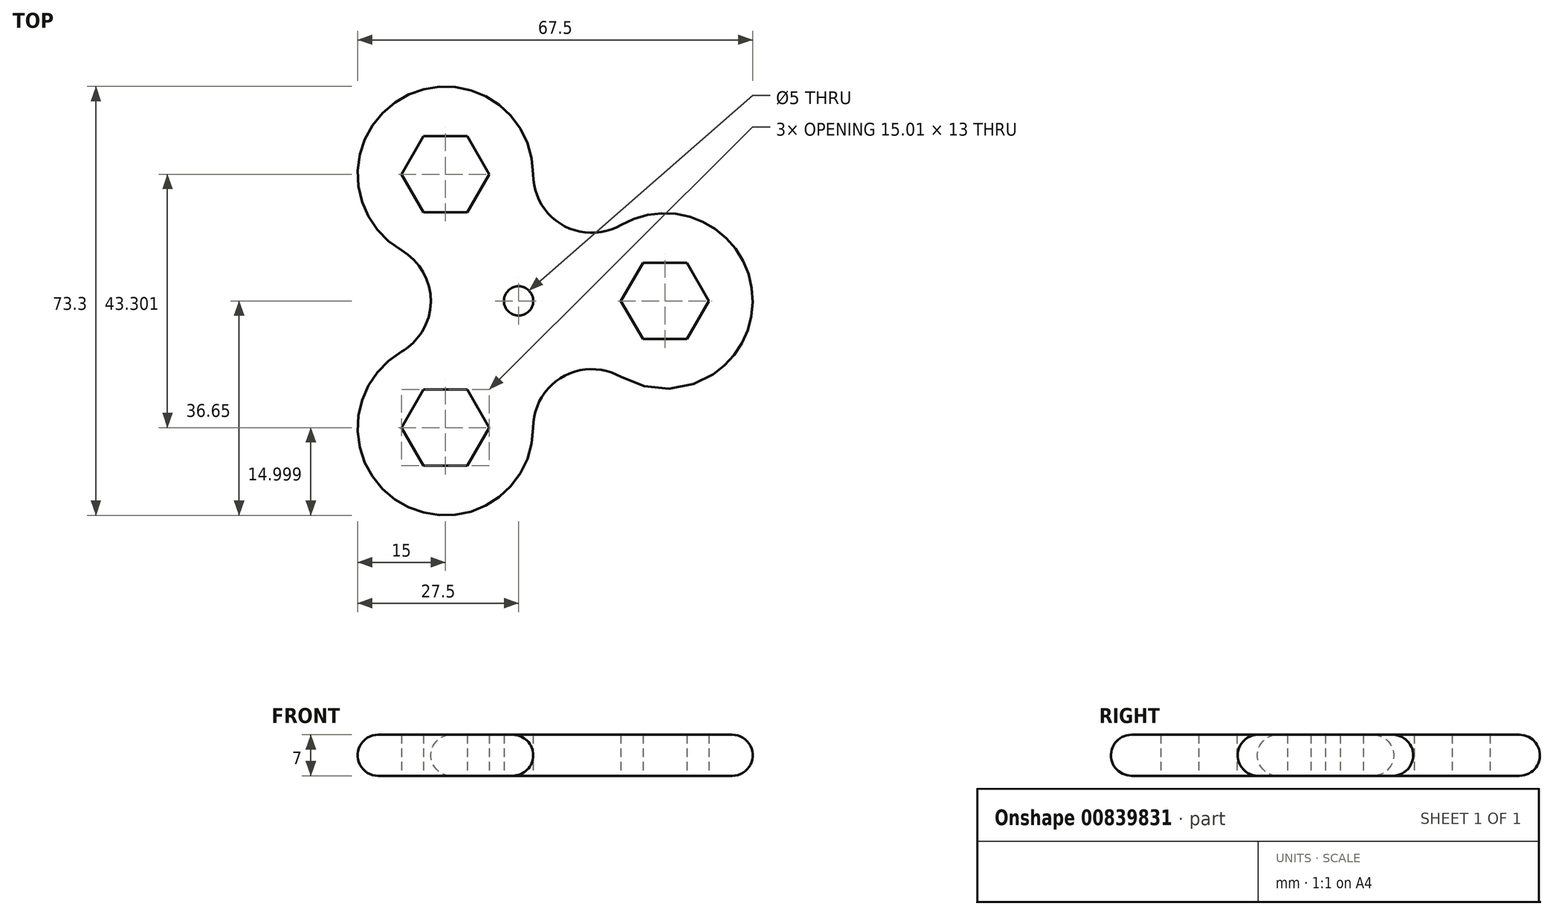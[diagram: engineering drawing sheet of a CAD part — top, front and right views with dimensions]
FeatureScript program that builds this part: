
annotation { "Feature Type Name" : "Feature", "Feature Type Description" : "" }
export const myFeature = defineFeature(function(context is Context, id is Id, definition is map)
    precondition{}
    {
        {
            var Q0;
            Q0=qCreatedBy(makeId("Top.planeOp"),FACE);
            var sketch = newSketch(context, id + "F0", { "sketchPlane" : qUnion([Q0])});
            skLineSegment(sketch, "E0", {"start": v(0, 0) * mm, "end": v(25, 0) * mm, "construction": true});
            skArc(sketch, "E1", {"start": v(17.5, -13) * mm, "mid": v(40, 0) * mm, "end": v(17.5, 13) * mm});
            skArc(sketch, "E2.1.1", {"start": v(2.5, 21.65) * mm, "mid": v(-20, 34.64) * mm, "end": v(-20, 8.66) * mm});
            skLineSegment(sketch, "E2.1.2", {"start": v(0, 0) * mm, "end": v(-12.5, 21.65) * mm, "construction": true});
            skArc(sketch, "E2.2.1", {"start": v(-20, -8.66) * mm, "mid": v(-20, -34.64) * mm, "end": v(2.5, -21.65) * mm});
            skLineSegment(sketch, "E2.2.2", {"start": v(0, 0) * mm, "end": v(-12.5, -21.65) * mm, "construction": true});
            skPoint(sketch, "E2.center", {"position": v(0, 0) * mm});
            skArc(sketch, "E3", {"start": v(2.5, 21.65) * mm, "mid": v(7.5, 13) * mm, "end": v(17.5, 13) * mm});
            skArc(sketch, "E4.1.0", {"start": v(-20, -8.66) * mm, "mid": v(-15, 0) * mm, "end": v(-20, 8.66) * mm});
            skArc(sketch, "E4.2.0", {"start": v(17.5, -13) * mm, "mid": v(7.5, -13) * mm, "end": v(2.5, -21.65) * mm});
            skCircle(sketch, "E5.cCircle", {"center": v(-12.5, -21.65) * mm, "radius": 6.5 * mm, "construction": true});
            skLineSegment(sketch, "E5.0", {"start": v(-8.75, -15.15) * mm, "end": v(-5, -21.65) * mm});
            skLineSegment(sketch, "E5.1", {"start": v(-5, -21.65) * mm, "end": v(-8.75, -28.15) * mm});
            skLineSegment(sketch, "E5.2", {"start": v(-8.75, -28.15) * mm, "end": v(-16.25, -28.15) * mm});
            skLineSegment(sketch, "E5.3", {"start": v(-16.25, -28.15) * mm, "end": v(-20, -21.65) * mm});
            skLineSegment(sketch, "E5.4", {"start": v(-20, -21.65) * mm, "end": v(-16.25, -15.15) * mm});
            skLineSegment(sketch, "E5.5", {"start": v(-16.25, -15.15) * mm, "end": v(-8.75, -15.15) * mm});
            skPoint(sketch, "E5.0.midPoint", {"position": v(-6.87, -18.4) * mm});
            skLineSegment(sketch, "E6.1.0", {"start": v(32.5, 0) * mm, "end": v(28.75, -6.5) * mm});
            skPoint(sketch, "E6.1.1", {"position": v(19.37, 3.25) * mm});
            skLineSegment(sketch, "E6.1.2", {"start": v(28.75, -6.5) * mm, "end": v(21.25, -6.5) * mm});
            skCircle(sketch, "E6.1.3", {"center": v(25, 0) * mm, "radius": 6.5 * mm, "construction": true});
            skLineSegment(sketch, "E6.1.4", {"start": v(28.75, 6.5) * mm, "end": v(32.5, 0) * mm});
            skLineSegment(sketch, "E6.1.5", {"start": v(21.25, -6.5) * mm, "end": v(17.5, 0) * mm});
            skLineSegment(sketch, "E6.1.6", {"start": v(17.5, 0) * mm, "end": v(21.25, 6.5) * mm});
            skLineSegment(sketch, "E6.1.7", {"start": v(21.25, 6.5) * mm, "end": v(28.75, 6.5) * mm});
            skLineSegment(sketch, "E6.2.0", {"start": v(-16.25, 28.15) * mm, "end": v(-8.75, 28.15) * mm});
            skPoint(sketch, "E6.2.1", {"position": v(-12.5, 15.15) * mm});
            skLineSegment(sketch, "E6.2.2", {"start": v(-8.75, 28.15) * mm, "end": v(-5, 21.65) * mm});
            skCircle(sketch, "E6.2.3", {"center": v(-12.5, 21.65) * mm, "radius": 6.5 * mm, "construction": true});
            skLineSegment(sketch, "E6.2.4", {"start": v(-20, 21.65) * mm, "end": v(-16.25, 28.15) * mm});
            skLineSegment(sketch, "E6.2.5", {"start": v(-5, 21.65) * mm, "end": v(-8.75, 15.15) * mm});
            skLineSegment(sketch, "E6.2.6", {"start": v(-8.75, 15.15) * mm, "end": v(-16.25, 15.15) * mm});
            skLineSegment(sketch, "E6.2.7", {"start": v(-16.25, 15.15) * mm, "end": v(-20, 21.65) * mm});
            skCircle(sketch, "E7", {"center": v(0, 0) * mm, "radius": 2.5 * mm});
            skSolve(sketch);
        }
        {
            var Q0;
            Q0=qSketchRegion(id+"F0",true);
            extrude(context, id + "F1", {"entities" : qUnion([Q0]), "depth" : 7 * mm, "offsetDistance" : 25 * mm});
        }
        {
            var Q0;
            Q0=makeQuery(id+"F1.opExtrude","CAP_EDGE",EDGE,{"disambiguationData":[OSD([sQuery(id+"F0.wireOp",EDGE,"E2.1.1")])],"isStart":false});
            var Q1;
            Q1=makeQuery(id+"F1.opExtrude","CAP_EDGE",EDGE,{"disambiguationData":[OSD([sQuery(id+"F0.wireOp",EDGE,"E3")])],"isStart":true});
            fillet(context, id + "F2", {"entities" : qUnion([Q0, Q1]), "radius" : 3.5 * mm, "tangentPropagation" : true, "allowEdgeOverflow" : false});
        }
    });
